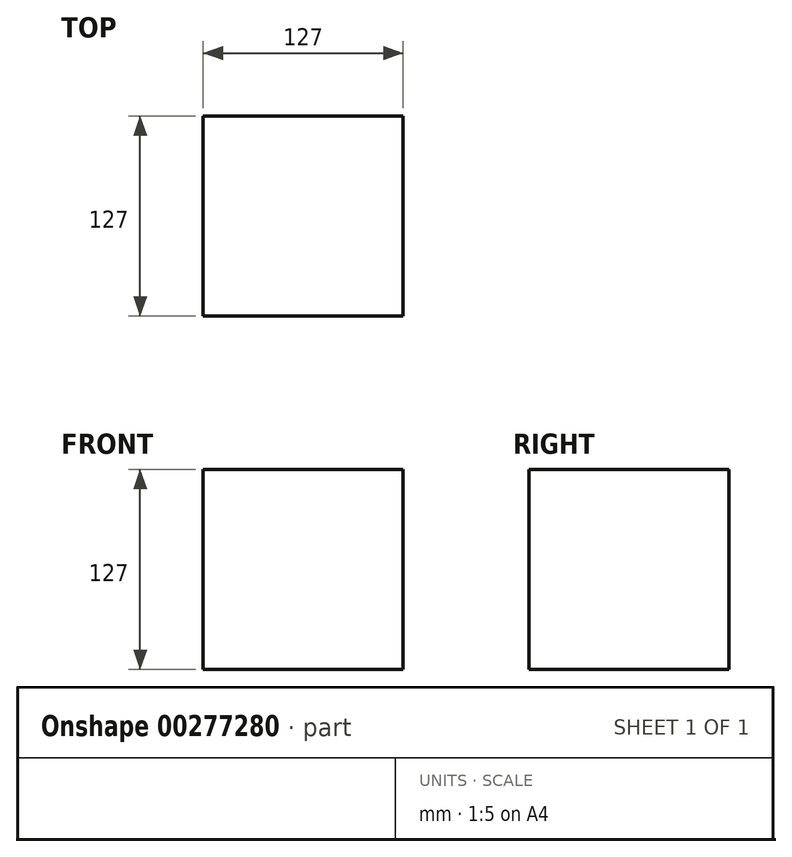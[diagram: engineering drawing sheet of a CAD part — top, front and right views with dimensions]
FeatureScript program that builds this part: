
annotation { "Feature Type Name" : "Feature", "Feature Type Description" : "" }
export const myFeature = defineFeature(function(context is Context, id is Id, definition is map)
    precondition{}
    {
        {
            var Q0;
            Q0=qCreatedBy(makeId("Top.planeOp"),FACE);
            var sketch = newSketch(context, id + "F0", { "sketchPlane" : qUnion([Q0])});
            skLineSegment(sketch, "E0.bottom", {"start": v(63.5, 63.5) * mm, "end": v(-63.5, 63.5) * mm});
            skLineSegment(sketch, "E0.top", {"start": v(63.5, -63.5) * mm, "end": v(-63.5, -63.5) * mm});
            skLineSegment(sketch, "E0.left", {"start": v(63.5, 63.5) * mm, "end": v(63.5, -63.5) * mm});
            skLineSegment(sketch, "E0.right", {"start": v(-63.5, 63.5) * mm, "end": v(-63.5, -63.5) * mm});
            skPoint(sketch, "E0.middle", {"position": v(0, 0) * mm});
            skSolve(sketch);
        }
        {
            var Q0;
            Q0 = qSketchRegion(id + "F0", true);
            extrude(context, id + "F1", {"entities" : qUnion([Q0]), "endBound" : BoundingType.SYMMETRIC, "depth" : 127 * mm});
        }
    });
